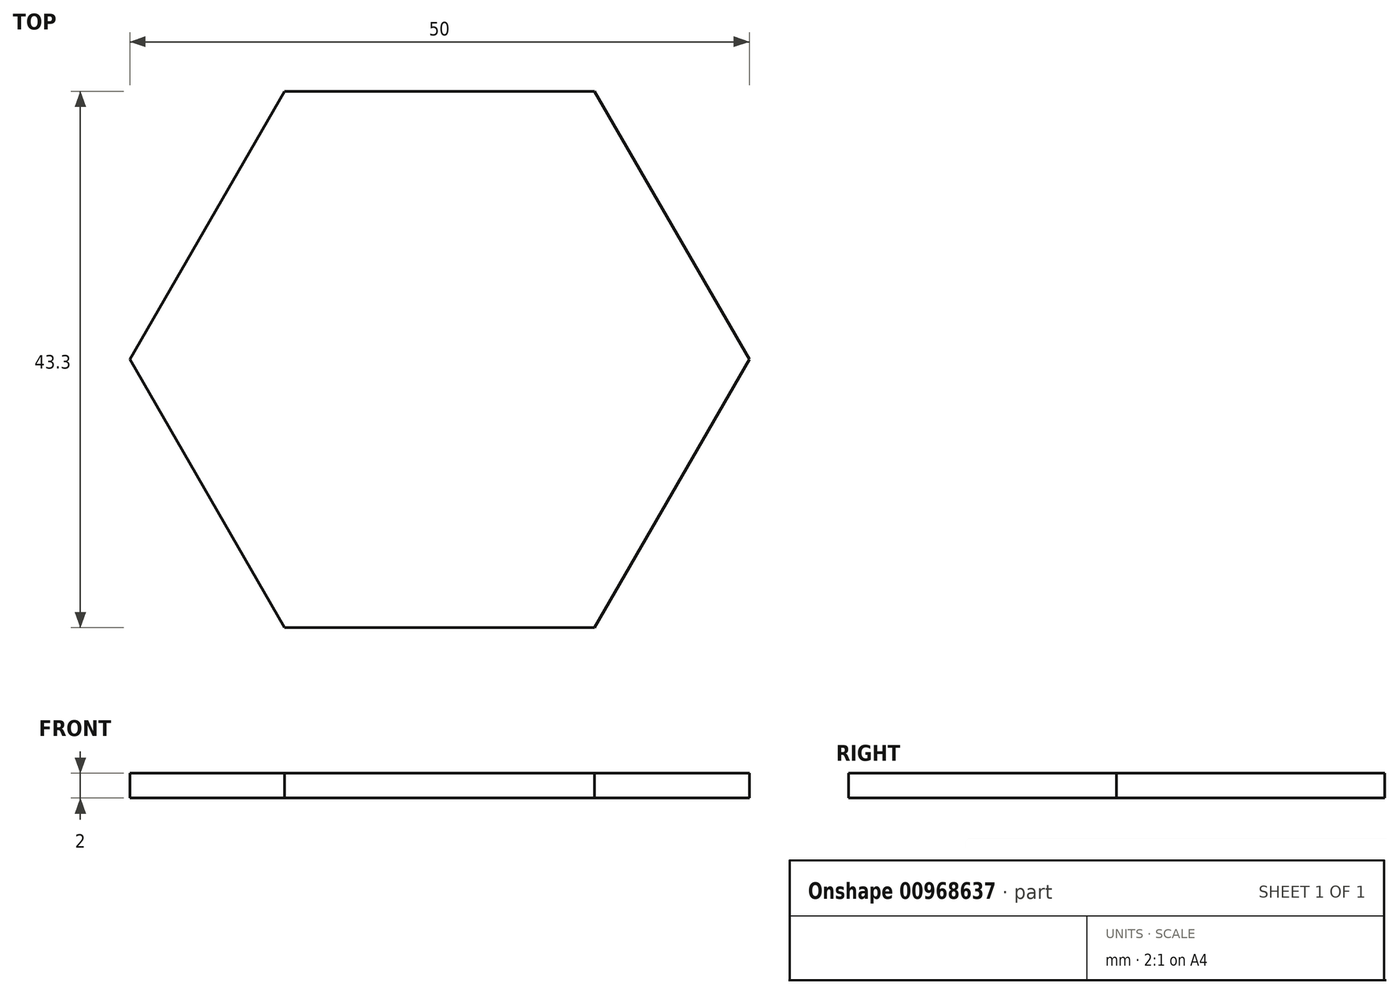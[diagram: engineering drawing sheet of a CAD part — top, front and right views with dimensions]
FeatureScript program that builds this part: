
annotation { "Feature Type Name" : "Feature", "Feature Type Description" : "" }
export const myFeature = defineFeature(function(context is Context, id is Id, definition is map)
    precondition{}
    {
        {
            var Q0;
            Q0=qCreatedBy(makeId("Top.planeOp"),FACE);
            var sketch = newSketch(context, id + "F0", { "sketchPlane" : qUnion([Q0])});
            skCircle(sketch, "E0.cCircle", {"center": v(0, 0) * mm, "radius": 25 * mm, "construction": true});
            skLineSegment(sketch, "E0.0", {"start": v(25, 0) * mm, "end": v(12.5, -21.65) * mm});
            skLineSegment(sketch, "E0.1", {"start": v(12.5, -21.65) * mm, "end": v(-12.5, -21.65) * mm});
            skLineSegment(sketch, "E0.2", {"start": v(-12.5, -21.65) * mm, "end": v(-25, 0) * mm});
            skLineSegment(sketch, "E0.3", {"start": v(-25, 0) * mm, "end": v(-12.5, 21.65) * mm});
            skLineSegment(sketch, "E0.4", {"start": v(-12.5, 21.65) * mm, "end": v(12.5, 21.65) * mm});
            skLineSegment(sketch, "E0.5", {"start": v(12.5, 21.65) * mm, "end": v(25, 0) * mm});
            skSolve(sketch);
        }
        {
            var Q0;
            Q0=makeQuery(id+"F0.imprint","IMPRINT",FACE,{"disambiguationData":[TD([[makeQuery(id+"F0.imprint","IMPRINT",EDGE,{"derivedFrom":sQuery(id+"F0.wireOp",EDGE,"E0.0")}),-1.0]])]});
            extrude(context, id + "F1", {"entities" : qUnion([Q0]), "depth" : 2 * mm, "offsetDistance" : 25 * mm});
        }
    });
